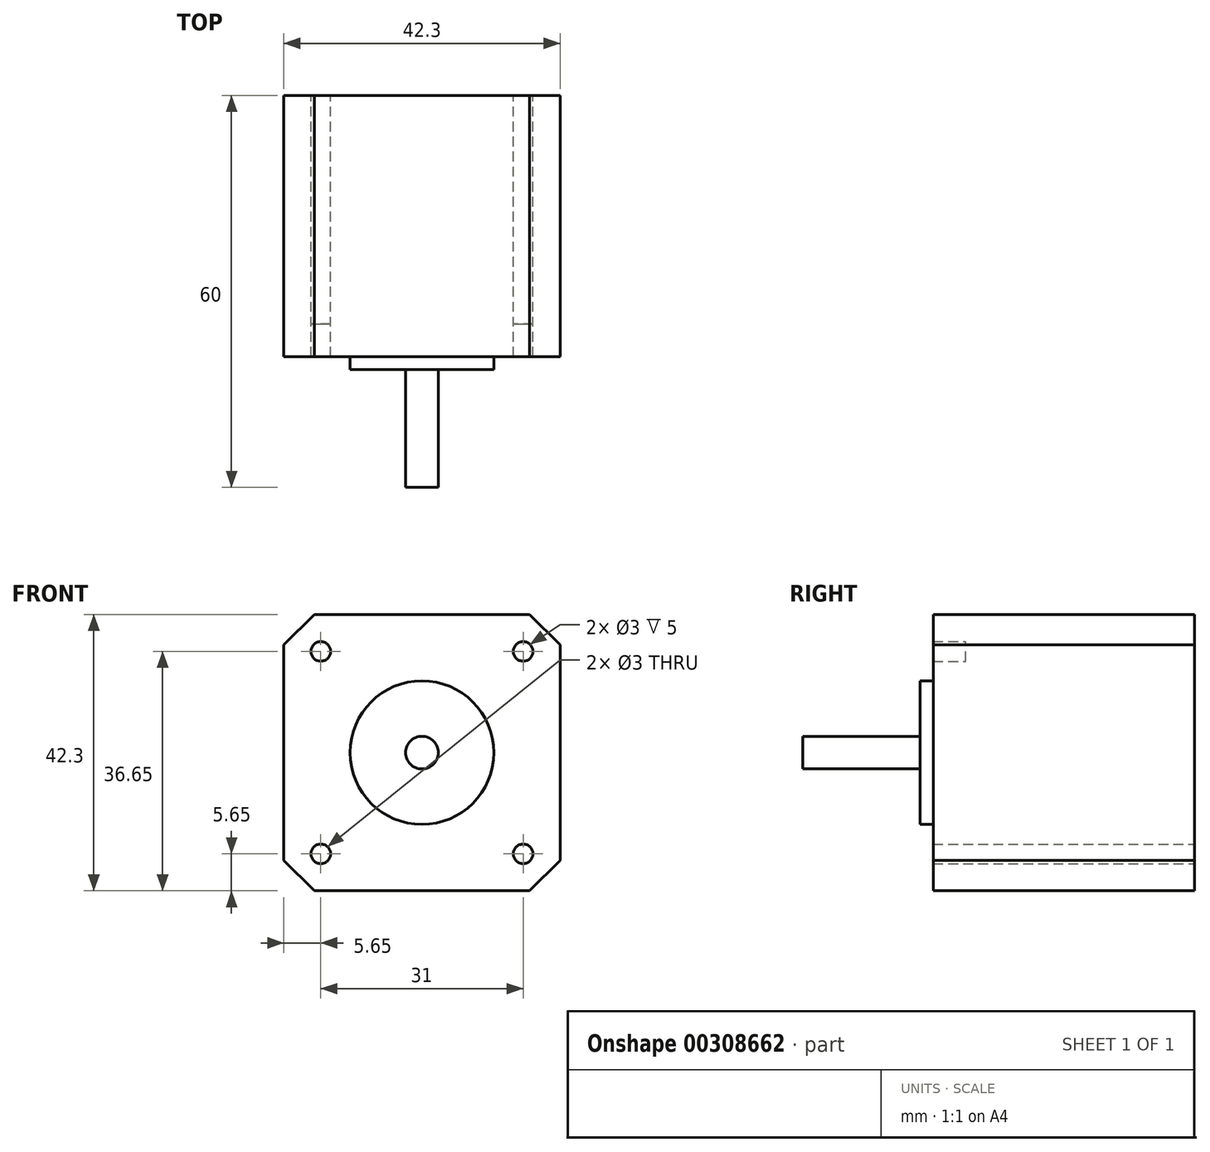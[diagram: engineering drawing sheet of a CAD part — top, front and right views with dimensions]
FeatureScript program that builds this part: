
annotation { "Feature Type Name" : "Feature", "Feature Type Description" : "" }
export const myFeature = defineFeature(function(context is Context, id is Id, definition is map)
    precondition{}
    {
        {
            var Q0;
            Q0=qCreatedBy(makeId("Front.planeOp"),FACE);
            var sketch = newSketch(context, id + "F0", { "sketchPlane" : qUnion([Q0])});
            skLineSegment(sketch, "E0.bottom", {"start": v(21.15, -21.15) * mm, "end": v(-21.15, -21.15) * mm});
            skLineSegment(sketch, "E0.top", {"start": v(21.15, 21.15) * mm, "end": v(-21.15, 21.15) * mm});
            skLineSegment(sketch, "E0.left", {"start": v(21.15, -21.15) * mm, "end": v(21.15, 21.15) * mm});
            skLineSegment(sketch, "E0.right", {"start": v(-21.15, -21.15) * mm, "end": v(-21.15, 21.15) * mm});
            skPoint(sketch, "E0.middle", {"position": v(0, 0) * mm});
            skCircle(sketch, "E1", {"center": v(15.5, 15.5) * mm, "radius": 1.5 * mm});
            skCircle(sketch, "E2", {"center": v(-15.5, 15.5) * mm, "radius": 1.5 * mm});
            skCircle(sketch, "E3.MirrorC", {"center": v(-15.5, -15.5) * mm, "radius": 1.5 * mm});
            skCircle(sketch, "E4.MirrorC", {"center": v(15.5, -15.5) * mm, "radius": 1.5 * mm});
            skCircle(sketch, "E5", {"center": v(0, 0) * mm, "radius": 11 * mm});
            skCircle(sketch, "E6", {"center": v(0, 0) * mm, "radius": 2.5 * mm});
            skLineSegment(sketch, "E7", {"start": v(-16.5, 21.15) * mm, "end": v(-21.15, 16.5) * mm});
            skLineSegment(sketch, "E8.MirrorCS", {"start": v(16.5, 21.15) * mm, "end": v(21.15, 16.5) * mm});
            skLineSegment(sketch, "E9.MirrorCS", {"start": v(-16.5, -21.15) * mm, "end": v(-21.15, -16.5) * mm});
            skLineSegment(sketch, "E10.MirrorCS", {"start": v(16.5, -21.15) * mm, "end": v(21.15, -16.5) * mm});
            skSolve(sketch);
        }
        {
            var Q0;
            Q0=makeQuery(id+"F0.imprint","IMPRINT",FACE,{"disambiguationData":[TD([[makeQuery(id+"F0.imprint","IMPRINT",EDGE,{"derivedFrom":sQuery(id+"F0.wireOp",EDGE,"E1")}),-1.0]])]});
            extrude(context, id + "F1", {"entities" : qUnion([Q0]), "depth" : 40 * mm});
        }
        {
            var Q0;
            Q0=makeQuery(id+"F0.imprint","IMPRINT",FACE,{"disambiguationData":[TD([[makeQuery(id+"F0.imprint","IMPRINT",EDGE,{"derivedFrom":sQuery(id+"F0.wireOp",EDGE,"E5")}),1.0]])]});
            extrude(context, id + "F2", {"entities" : qUnion([Q0]), "operationType" : NewBodyOperationType.ADD, "depth" : 42 * mm});
        }
        {
            var Q0;
            Q0=makeQuery(id+"F0.imprint","IMPRINT",FACE,{"disambiguationData":[TD([[makeQuery(id+"F0.imprint","IMPRINT",EDGE,{"derivedFrom":sQuery(id+"F0.wireOp",EDGE,"E6")}),1.0]])]});
            extrude(context, id + "F3", {"entities" : qUnion([Q0]), "operationType" : NewBodyOperationType.ADD, "depth" : 60 * mm});
        }
        {
            var Q0;
            Q0=makeQuery(id+"F0.imprint","IMPRINT",FACE,{"disambiguationData":[TD([[makeQuery(id+"F0.imprint","IMPRINT",EDGE,{"derivedFrom":sQuery(id+"F0.wireOp",EDGE,"E1")}),1.0]])]});
            var Q1;
            Q1=makeQuery(id+"F0.imprint","IMPRINT",FACE,{"disambiguationData":[TD([[makeQuery(id+"F0.imprint","IMPRINT",EDGE,{"derivedFrom":sQuery(id+"F0.wireOp",EDGE,"E2")}),1.0]])]});
            var Q2;
            Q2=makeQuery(id+"F0.imprint","IMPRINT",FACE,{"disambiguationData":[TD([[makeQuery(id+"F0.imprint","IMPRINT",EDGE,{"derivedFrom":sQuery(id+"F0.wireOp",EDGE,"E3.MirrorC")}),-1.0]])]});
            var Q3;
            Q3=makeQuery(id+"F0.imprint","IMPRINT",FACE,{"disambiguationData":[TD([[makeQuery(id+"F0.imprint","IMPRINT",EDGE,{"derivedFrom":sQuery(id+"F0.wireOp",EDGE,"E4.MirrorC")}),-1.0]])]});
            extrude(context, id + "F4", {"entities" : qUnion([Q0, Q1, Q2, Q3]), "operationType" : NewBodyOperationType.ADD, "depth" : 35 * mm});
        }
    });
